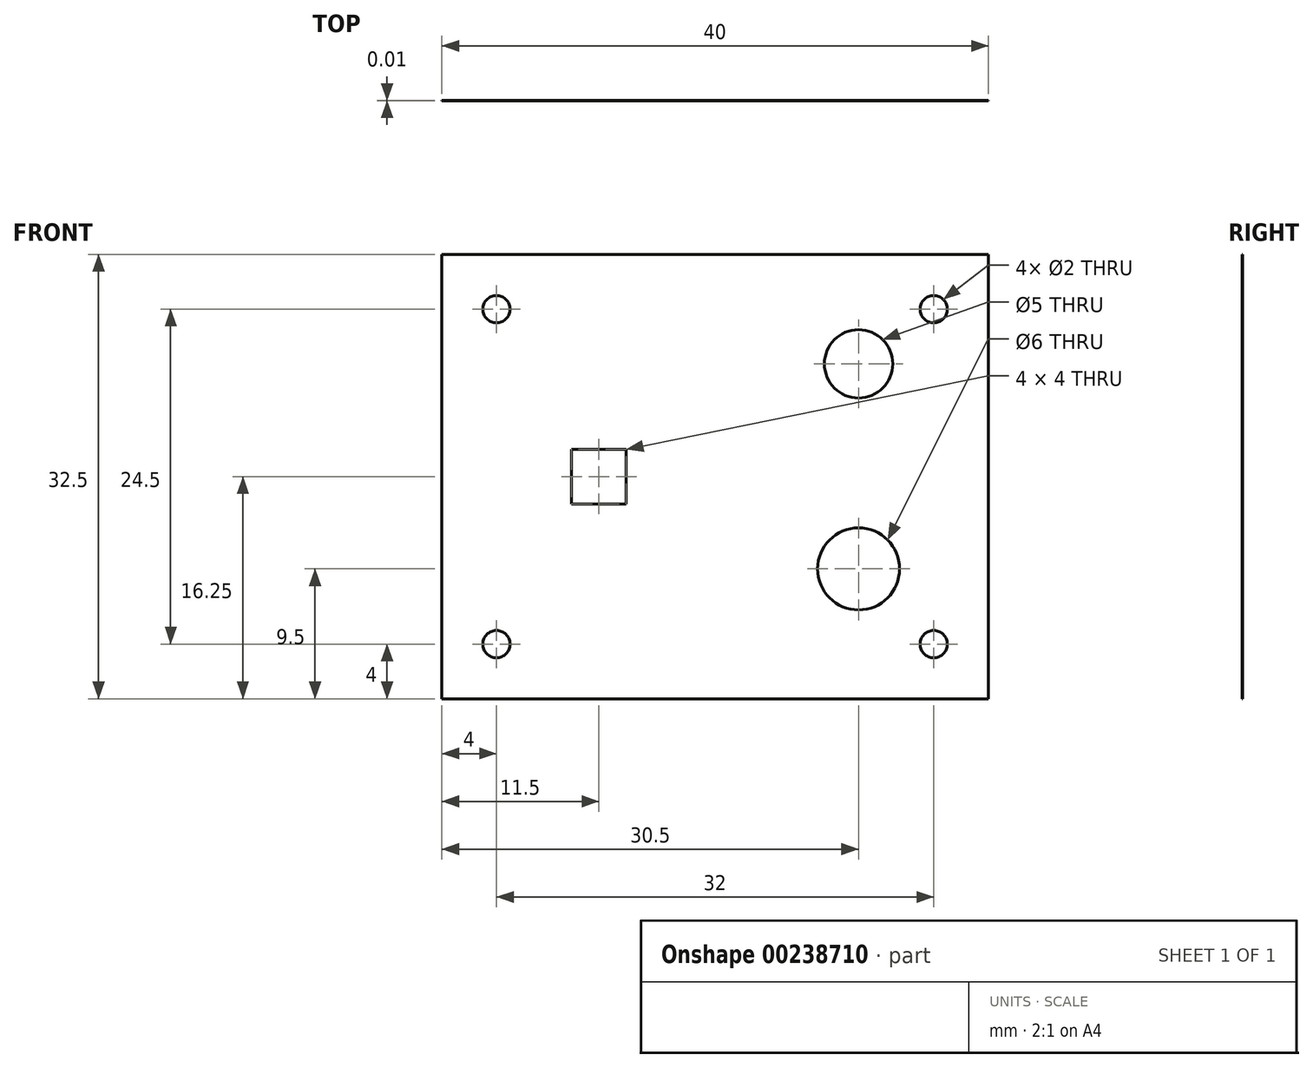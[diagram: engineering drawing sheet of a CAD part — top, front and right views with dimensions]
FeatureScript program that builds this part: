
annotation { "Feature Type Name" : "Feature", "Feature Type Description" : "" }
export const myFeature = defineFeature(function(context is Context, id is Id, definition is map)
    precondition{}
    {
        {
            var Q0;
            Q0=qCreatedBy(makeId("Front.planeOp"),FACE);
            var sketch = newSketch(context, id + "F0", { "sketchPlane" : qUnion([Q0])});
            skCircle(sketch, "E0", {"center": v(31.5, 16.25) * mm, "radius": 6.5 * mm, "construction": true});
            skCircle(sketch, "E1", {"center": v(50.5, 9.5) * mm, "radius": 4.5 * mm});
            skCircle(sketch, "E2", {"center": v(50.5, 9.5) * mm, "radius": 3 * mm});
            skCircle(sketch, "E3", {"center": v(50.5, 24.5) * mm, "radius": 3 * mm});
            skCircle(sketch, "E4", {"center": v(50.5, 24.5) * mm, "radius": 2.5 * mm});
            skLineSegment(sketch, "E5", {"start": v(50.5, 27.5) * mm, "end": v(50.5, 5) * mm, "construction": true});
            skPoint(sketch, "E6.positionSnap0", {"position": v(50.5, 16.25) * mm});
            skLineSegment(sketch, "E7.bottom", {"start": v(20, 32.5) * mm, "end": v(60, 32.5) * mm});
            skLineSegment(sketch, "E7.top", {"start": v(20, 0) * mm, "end": v(60, 0) * mm});
            skLineSegment(sketch, "E7.left", {"start": v(20, 32.5) * mm, "end": v(20, 0) * mm});
            skLineSegment(sketch, "E7.right", {"start": v(60, 32.5) * mm, "end": v(60, 0) * mm});
            skLineSegment(sketch, "E8", {"start": v(25.5, 22.25) * mm, "end": v(25.5, 23.75) * mm});
            skLineSegment(sketch, "E9", {"start": v(25.5, 23.75) * mm, "end": v(37.5, 23.75) * mm});
            skLineSegment(sketch, "E10", {"start": v(37.5, 23.75) * mm, "end": v(37.5, 22.25) * mm});
            skLineSegment(sketch, "E11", {"start": v(20, 16.25) * mm, "end": v(60, 16.25) * mm, "construction": true});
            skLineSegment(sketch, "E12.MirrorCS", {"start": v(37.5, 8.75) * mm, "end": v(37.5, 10.25) * mm});
            skLineSegment(sketch, "E13.MirrorCS", {"start": v(25.5, 8.75) * mm, "end": v(37.5, 8.75) * mm});
            skLineSegment(sketch, "E14.MirrorCS", {"start": v(25.5, 10.25) * mm, "end": v(25.5, 8.75) * mm});
            skLineSegment(sketch, "E15", {"start": v(55, 9.5) * mm, "end": v(60, 9.5) * mm, "construction": true});
            skLineSegment(sketch, "E16", {"start": v(46, 9.5) * mm, "end": v(46, 16.25) * mm, "construction": true});
            skLineSegment(sketch, "E17.bottom", {"start": v(37.5, 22.25) * mm, "end": v(25.5, 22.25) * mm});
            skLineSegment(sketch, "E17.top", {"start": v(37.5, 10.25) * mm, "end": v(25.5, 10.25) * mm});
            skLineSegment(sketch, "E17.left", {"start": v(37.5, 22.25) * mm, "end": v(37.5, 10.25) * mm});
            skLineSegment(sketch, "E17.right", {"start": v(25.5, 22.25) * mm, "end": v(25.5, 10.25) * mm});
            skLineSegment(sketch, "E18.bottom", {"start": v(29.5, 18.25) * mm, "end": v(33.5, 18.25) * mm});
            skLineSegment(sketch, "E18.top", {"start": v(29.5, 14.25) * mm, "end": v(33.5, 14.25) * mm});
            skLineSegment(sketch, "E18.left", {"start": v(29.5, 18.25) * mm, "end": v(29.5, 14.25) * mm});
            skLineSegment(sketch, "E18.right", {"start": v(33.5, 18.25) * mm, "end": v(33.5, 14.25) * mm});
            skLineSegment(sketch, "E19.1.0.0", {"start": v(97.5, 22.25) * mm, "end": v(85.5, 22.25) * mm});
            skCircle(sketch, "E19.1.0.1", {"center": v(110.5, 24.5) * mm, "radius": 2.5 * mm});
            skCircle(sketch, "E19.1.0.3", {"center": v(91.5, 16.25) * mm, "radius": 6.5 * mm, "construction": true});
            skLineSegment(sketch, "E19.1.0.4", {"start": v(120, 32.5) * mm, "end": v(120, 0) * mm});
            skLineSegment(sketch, "E19.1.0.5", {"start": v(80, 32.5) * mm, "end": v(120, 32.5) * mm});
            skLineSegment(sketch, "E19.1.0.6", {"start": v(89.5, 18.25) * mm, "end": v(89.5, 14.25) * mm});
            skLineSegment(sketch, "E19.1.0.7", {"start": v(89.5, 18.25) * mm, "end": v(93.5, 18.25) * mm});
            skLineSegment(sketch, "E19.1.0.8", {"start": v(97.5, 10.25) * mm, "end": v(85.5, 10.25) * mm});
            skLineSegment(sketch, "E19.1.0.9", {"start": v(85.5, 23.75) * mm, "end": v(97.5, 23.75) * mm});
            skCircle(sketch, "E19.1.0.10", {"center": v(110.5, 9.5) * mm, "radius": 4.5 * mm});
            skLineSegment(sketch, "E19.1.0.11", {"start": v(93.5, 18.25) * mm, "end": v(93.5, 14.25) * mm});
            skPoint(sketch, "E19.1.0.13", {"position": v(91.5, 16.25) * mm});
            skLineSegment(sketch, "E19.1.0.14", {"start": v(80, 32.5) * mm, "end": v(80, 0) * mm});
            skLineSegment(sketch, "E19.1.0.15", {"start": v(85.5, 8.75) * mm, "end": v(97.5, 8.75) * mm});
            skCircle(sketch, "E19.1.0.16", {"center": v(110.5, 9.5) * mm, "radius": 3 * mm});
            skCircle(sketch, "E19.1.0.17", {"center": v(110.5, 24.5) * mm, "radius": 3 * mm});
            skLineSegment(sketch, "E19.1.0.18", {"start": v(85.5, 22.25) * mm, "end": v(85.5, 10.25) * mm});
            skLineSegment(sketch, "E19.1.0.19", {"start": v(97.5, 22.25) * mm, "end": v(97.5, 10.25) * mm});
            skLineSegment(sketch, "E19.1.0.20", {"start": v(80, 0) * mm, "end": v(120, 0) * mm});
            skLineSegment(sketch, "E19.1.0.22", {"start": v(89.5, 14.25) * mm, "end": v(93.5, 14.25) * mm});
            skPoint(sketch, "E19.1.0.23", {"position": v(91.5, 16.25) * mm});
            skLineSegment(sketch, "E19.1.0.24", {"start": v(97.5, 23.75) * mm, "end": v(97.5, 22.25) * mm});
            skLineSegment(sketch, "E19.1.0.25", {"start": v(85.5, 22.25) * mm, "end": v(85.5, 23.75) * mm});
            skLineSegment(sketch, "E19.1.0.26", {"start": v(85.5, 10.25) * mm, "end": v(85.5, 8.75) * mm});
            skLineSegment(sketch, "E19.1.0.27", {"start": v(97.5, 8.75) * mm, "end": v(97.5, 10.25) * mm});
            skLineSegment(sketch, "E19.2.0.0", {"start": v(157.5, 22.25) * mm, "end": v(145.5, 22.25) * mm});
            skCircle(sketch, "E19.2.0.1", {"center": v(170.5, 24.5) * mm, "radius": 2.5 * mm});
            skCircle(sketch, "E19.2.0.3", {"center": v(151.5, 16.25) * mm, "radius": 6.5 * mm, "construction": true});
            skLineSegment(sketch, "E19.2.0.4", {"start": v(180, 32.5) * mm, "end": v(180, 0) * mm});
            skLineSegment(sketch, "E19.2.0.5", {"start": v(140, 32.5) * mm, "end": v(180, 32.5) * mm});
            skLineSegment(sketch, "E19.2.0.6", {"start": v(149.5, 18.25) * mm, "end": v(149.5, 14.25) * mm});
            skLineSegment(sketch, "E19.2.0.7", {"start": v(149.5, 18.25) * mm, "end": v(153.5, 18.25) * mm});
            skLineSegment(sketch, "E19.2.0.8", {"start": v(157.5, 10.25) * mm, "end": v(145.5, 10.25) * mm});
            skLineSegment(sketch, "E19.2.0.9", {"start": v(145.5, 23.75) * mm, "end": v(157.5, 23.75) * mm});
            skCircle(sketch, "E19.2.0.10", {"center": v(170.5, 9.5) * mm, "radius": 4.5 * mm});
            skLineSegment(sketch, "E19.2.0.11", {"start": v(153.5, 18.25) * mm, "end": v(153.5, 14.25) * mm});
            skPoint(sketch, "E19.2.0.13", {"position": v(151.5, 16.25) * mm});
            skLineSegment(sketch, "E19.2.0.14", {"start": v(140, 32.5) * mm, "end": v(140, 0) * mm});
            skLineSegment(sketch, "E19.2.0.15", {"start": v(145.5, 8.75) * mm, "end": v(157.5, 8.75) * mm});
            skCircle(sketch, "E19.2.0.16", {"center": v(170.5, 9.5) * mm, "radius": 3 * mm});
            skCircle(sketch, "E19.2.0.17", {"center": v(170.5, 24.5) * mm, "radius": 3 * mm});
            skLineSegment(sketch, "E19.2.0.18", {"start": v(145.5, 22.25) * mm, "end": v(145.5, 10.25) * mm});
            skLineSegment(sketch, "E19.2.0.19", {"start": v(157.5, 22.25) * mm, "end": v(157.5, 10.25) * mm});
            skLineSegment(sketch, "E19.2.0.20", {"start": v(140, 0) * mm, "end": v(180, 0) * mm});
            skLineSegment(sketch, "E19.2.0.22", {"start": v(149.5, 14.25) * mm, "end": v(153.5, 14.25) * mm});
            skPoint(sketch, "E19.2.0.23", {"position": v(151.5, 16.25) * mm});
            skLineSegment(sketch, "E19.2.0.24", {"start": v(157.5, 23.75) * mm, "end": v(157.5, 22.25) * mm});
            skLineSegment(sketch, "E19.2.0.25", {"start": v(145.5, 22.25) * mm, "end": v(145.5, 23.75) * mm});
            skLineSegment(sketch, "E19.2.0.26", {"start": v(145.5, 10.25) * mm, "end": v(145.5, 8.75) * mm});
            skLineSegment(sketch, "E19.2.0.27", {"start": v(157.5, 8.75) * mm, "end": v(157.5, 10.25) * mm});
            skLineSegment(sketch, "E19.3.0.0", {"start": v(217.5, 22.25) * mm, "end": v(205.5, 22.25) * mm});
            skCircle(sketch, "E19.3.0.1", {"center": v(230.5, 24.5) * mm, "radius": 2.5 * mm});
            skCircle(sketch, "E19.3.0.3", {"center": v(211.5, 16.25) * mm, "radius": 6.5 * mm, "construction": true});
            skLineSegment(sketch, "E19.3.0.4", {"start": v(240, 32.5) * mm, "end": v(240, 0) * mm});
            skLineSegment(sketch, "E19.3.0.5", {"start": v(200, 32.5) * mm, "end": v(240, 32.5) * mm});
            skLineSegment(sketch, "E19.3.0.6", {"start": v(209.5, 18.25) * mm, "end": v(209.5, 14.25) * mm});
            skLineSegment(sketch, "E19.3.0.7", {"start": v(209.5, 18.25) * mm, "end": v(213.5, 18.25) * mm});
            skLineSegment(sketch, "E19.3.0.8", {"start": v(217.5, 10.25) * mm, "end": v(205.5, 10.25) * mm});
            skLineSegment(sketch, "E19.3.0.9", {"start": v(205.5, 23.75) * mm, "end": v(217.5, 23.75) * mm});
            skCircle(sketch, "E19.3.0.10", {"center": v(230.5, 9.5) * mm, "radius": 4.5 * mm});
            skLineSegment(sketch, "E19.3.0.11", {"start": v(213.5, 18.25) * mm, "end": v(213.5, 14.25) * mm});
            skPoint(sketch, "E19.3.0.13", {"position": v(211.5, 16.25) * mm});
            skLineSegment(sketch, "E19.3.0.14", {"start": v(200, 32.5) * mm, "end": v(200, 0) * mm});
            skLineSegment(sketch, "E19.3.0.15", {"start": v(205.5, 8.75) * mm, "end": v(217.5, 8.75) * mm});
            skCircle(sketch, "E19.3.0.16", {"center": v(230.5, 9.5) * mm, "radius": 3 * mm});
            skCircle(sketch, "E19.3.0.17", {"center": v(230.5, 24.5) * mm, "radius": 3 * mm});
            skLineSegment(sketch, "E19.3.0.18", {"start": v(205.5, 22.25) * mm, "end": v(205.5, 10.25) * mm});
            skLineSegment(sketch, "E19.3.0.19", {"start": v(217.5, 22.25) * mm, "end": v(217.5, 10.25) * mm});
            skLineSegment(sketch, "E19.3.0.20", {"start": v(200, 0) * mm, "end": v(240, 0) * mm});
            skLineSegment(sketch, "E19.3.0.22", {"start": v(209.5, 14.25) * mm, "end": v(213.5, 14.25) * mm});
            skPoint(sketch, "E19.3.0.23", {"position": v(211.5, 16.25) * mm});
            skLineSegment(sketch, "E19.3.0.24", {"start": v(217.5, 23.75) * mm, "end": v(217.5, 22.25) * mm});
            skLineSegment(sketch, "E19.3.0.25", {"start": v(205.5, 22.25) * mm, "end": v(205.5, 23.75) * mm});
            skLineSegment(sketch, "E19.3.0.26", {"start": v(205.5, 10.25) * mm, "end": v(205.5, 8.75) * mm});
            skLineSegment(sketch, "E19.3.0.27", {"start": v(217.5, 8.75) * mm, "end": v(217.5, 10.25) * mm});
            skLineSegment(sketch, "E19.direction1", {"start": v(20, 0) * mm, "end": v(80, 0) * mm, "construction": true});
            skLineSegment(sketch, "E20.bottom", {"start": v(0, -97.5) * mm, "end": v(260, -97.5) * mm});
            skLineSegment(sketch, "E20.top", {"start": v(0, 52.5) * mm, "end": v(260, 52.5) * mm});
            skLineSegment(sketch, "E20.left", {"start": v(0, -97.5) * mm, "end": v(0, 52.5) * mm});
            skLineSegment(sketch, "E20.right", {"start": v(260, -97.5) * mm, "end": v(260, 52.5) * mm});
            skLineSegment(sketch, "E21", {"start": v(120, 0) * mm, "end": v(140, 0) * mm, "construction": true});
            skLineSegment(sketch, "E22.bottom", {"start": v(149.5, -42.5) * mm, "end": v(103.5, -42.5) * mm});
            skLineSegment(sketch, "E22.top", {"start": v(149.5, -69.5) * mm, "end": v(103.5, -69.5) * mm});
            skLineSegment(sketch, "E22.right", {"start": v(103.5, -42.5) * mm, "end": v(103.5, -69.5) * mm});
            skLineSegment(sketch, "E23.bottom", {"start": v(156.5, -42.5) * mm, "end": v(150.5, -42.5) * mm});
            skLineSegment(sketch, "E23.top", {"start": v(156.5, -69.5) * mm, "end": v(150.5, -69.5) * mm});
            skLineSegment(sketch, "E23.left", {"start": v(156.5, -42.5) * mm, "end": v(156.5, -69.5) * mm});
            skLineSegment(sketch, "E24.bottom", {"start": v(157.5, -70.5) * mm, "end": v(102.5, -70.5) * mm});
            skLineSegment(sketch, "E24.top", {"start": v(157.5, -41.5) * mm, "end": v(102.5, -41.5) * mm});
            skLineSegment(sketch, "E24.left", {"start": v(157.5, -70.5) * mm, "end": v(157.5, -41.5) * mm});
            skLineSegment(sketch, "E24.right", {"start": v(102.5, -70.5) * mm, "end": v(102.5, -41.5) * mm});
            skCircle(sketch, "E25", {"center": v(148, -29.5) * mm, "radius": 5 * mm});
            skCircle(sketch, "E26", {"center": v(112, -29.5) * mm, "radius": 5 * mm});
            skLineSegment(sketch, "E27", {"start": v(148, -29.5) * mm, "end": v(112, -29.5) * mm, "construction": true});
            skLineSegment(sketch, "E28", {"start": v(150.5, -67.5) * mm, "end": v(149.5, -67.5) * mm});
            skLineSegment(sketch, "E29", {"start": v(150.5, -44.5) * mm, "end": v(149.5, -44.5) * mm});
            skLineSegment(sketch, "E30", {"start": v(150.5, -69.5) * mm, "end": v(150.5, -67.5) * mm});
            skLineSegment(sketch, "E31", {"start": v(149.5, -69.5) * mm, "end": v(149.5, -67.5) * mm});
            skLineSegment(sketch, "E32", {"start": v(150.5, -44.5) * mm, "end": v(150.5, -42.5) * mm});
            skLineSegment(sketch, "E33", {"start": v(149.5, -44.5) * mm, "end": v(149.5, -42.5) * mm});
            skLineSegment(sketch, "E34.bottom", {"start": v(100, -77.5) * mm, "end": v(100, -17.5) * mm});
            skLineSegment(sketch, "E34.top", {"start": v(160, -77.5) * mm, "end": v(160, -17.5) * mm});
            skLineSegment(sketch, "E34.left", {"start": v(100, -77.5) * mm, "end": v(160, -77.5) * mm});
            skLineSegment(sketch, "E34.right", {"start": v(100, -17.5) * mm, "end": v(160, -17.5) * mm});
            skPoint(sketch, "E35", {"position": v(130, -29.5) * mm});
            skLineSegment(sketch, "E36", {"start": v(130, -41.5) * mm, "end": v(130, -17.5) * mm, "construction": true});
            skLineSegment(sketch, "E37", {"start": v(160, -70.5) * mm, "end": v(157.5, -70.5) * mm, "construction": true});
            skLineSegment(sketch, "E38", {"start": v(102.5, -70.5) * mm, "end": v(100, -70.5) * mm, "construction": true});
            skLineSegment(sketch, "E39", {"start": v(148, -24.5) * mm, "end": v(148, -17.5) * mm, "construction": true});
            skLineSegment(sketch, "E40", {"start": v(148, -70.5) * mm, "end": v(148, -77.5) * mm, "construction": true});
            skLineSegment(sketch, "E41", {"start": v(153, -29.5) * mm, "end": v(160, -29.5) * mm, "construction": true});
            skLineSegment(sketch, "E42", {"start": v(148, -34.5) * mm, "end": v(148, -41.5) * mm, "construction": true});
            skLineSegment(sketch, "E43", {"start": v(130, 0) * mm, "end": v(130, -97.5) * mm, "construction": true});
            skLineSegment(sketch, "E44.1.0.0", {"start": v(180, -77.5) * mm, "end": v(180, -17.5) * mm});
            skLineSegment(sketch, "E44.1.0.1", {"start": v(240, -77.5) * mm, "end": v(240, -17.5) * mm});
            skLineSegment(sketch, "E44.1.0.2", {"start": v(237.5, -70.5) * mm, "end": v(182.5, -70.5) * mm});
            skLineSegment(sketch, "E44.1.0.3", {"start": v(237.5, -70.5) * mm, "end": v(237.5, -41.5) * mm});
            skLineSegment(sketch, "E44.1.0.4", {"start": v(180, -17.5) * mm, "end": v(240, -17.5) * mm});
            skLineSegment(sketch, "E44.1.0.5", {"start": v(183.5, -42.5) * mm, "end": v(183.5, -69.5) * mm});
            skPoint(sketch, "E44.1.0.6", {"position": v(210, -29.5) * mm});
            skCircle(sketch, "E44.1.0.7", {"center": v(228, -29.5) * mm, "radius": 5 * mm});
            skLineSegment(sketch, "E44.1.0.8", {"start": v(233, -29.5) * mm, "end": v(240, -29.5) * mm, "construction": true});
            skLineSegment(sketch, "E44.1.0.9", {"start": v(229.5, -69.5) * mm, "end": v(183.5, -69.5) * mm});
            skLineSegment(sketch, "E44.1.0.10", {"start": v(210, -41.5) * mm, "end": v(210, -17.5) * mm, "construction": true});
            skLineSegment(sketch, "E44.1.0.11", {"start": v(228, -70.5) * mm, "end": v(228, -77.5) * mm, "construction": true});
            skLineSegment(sketch, "E44.1.0.12", {"start": v(237.5, -41.5) * mm, "end": v(182.5, -41.5) * mm});
            skLineSegment(sketch, "E44.1.0.13", {"start": v(228, -24.5) * mm, "end": v(228, -17.5) * mm, "construction": true});
            skLineSegment(sketch, "E44.1.0.14", {"start": v(229.5, -42.5) * mm, "end": v(183.5, -42.5) * mm});
            skCircle(sketch, "E44.1.0.15", {"center": v(192, -29.5) * mm, "radius": 5 * mm});
            skLineSegment(sketch, "E44.1.0.16", {"start": v(228, -34.5) * mm, "end": v(228, -41.5) * mm, "construction": true});
            skLineSegment(sketch, "E44.1.0.17", {"start": v(180, -77.5) * mm, "end": v(240, -77.5) * mm});
            skLineSegment(sketch, "E44.1.0.18", {"start": v(236.5, -42.5) * mm, "end": v(236.5, -69.5) * mm});
            skLineSegment(sketch, "E44.1.0.19", {"start": v(182.5, -70.5) * mm, "end": v(182.5, -41.5) * mm});
            skLineSegment(sketch, "E44.1.0.20", {"start": v(228, -29.5) * mm, "end": v(192, -29.5) * mm, "construction": true});
            skLineSegment(sketch, "E44.1.0.21", {"start": v(240, -70.5) * mm, "end": v(237.5, -70.5) * mm, "construction": true});
            skLineSegment(sketch, "E44.1.0.22", {"start": v(182.5, -70.5) * mm, "end": v(180, -70.5) * mm, "construction": true});
            skLineSegment(sketch, "E44.1.0.23", {"start": v(229.5, -44.5) * mm, "end": v(229.5, -42.5) * mm});
            skLineSegment(sketch, "E44.1.0.24", {"start": v(236.5, -42.5) * mm, "end": v(230.5, -42.5) * mm});
            skLineSegment(sketch, "E44.1.0.25", {"start": v(230.5, -44.5) * mm, "end": v(230.5, -42.5) * mm});
            skLineSegment(sketch, "E44.1.0.26", {"start": v(236.5, -69.5) * mm, "end": v(230.5, -69.5) * mm});
            skLineSegment(sketch, "E44.1.0.27", {"start": v(230.5, -69.5) * mm, "end": v(230.5, -67.5) * mm});
            skLineSegment(sketch, "E44.1.0.28", {"start": v(230.5, -44.5) * mm, "end": v(229.5, -44.5) * mm});
            skLineSegment(sketch, "E44.1.0.29", {"start": v(229.5, -69.5) * mm, "end": v(229.5, -67.5) * mm});
            skLineSegment(sketch, "E44.1.0.30", {"start": v(230.5, -67.5) * mm, "end": v(229.5, -67.5) * mm});
            skLineSegment(sketch, "E44.direction1", {"start": v(100, -77.5) * mm, "end": v(180, -77.5) * mm, "construction": true});
            skLineSegment(sketch, "E45.bottom", {"start": v(45, -28) * mm, "end": v(45, -74) * mm});
            skLineSegment(sketch, "E45.top", {"start": v(72, -28) * mm, "end": v(72, -74) * mm});
            skLineSegment(sketch, "E45.right", {"start": v(45, -74) * mm, "end": v(72, -74) * mm});
            skLineSegment(sketch, "E46.bottom", {"start": v(45, -21) * mm, "end": v(45, -27) * mm});
            skLineSegment(sketch, "E46.top", {"start": v(72, -21) * mm, "end": v(72, -27) * mm});
            skLineSegment(sketch, "E46.left", {"start": v(45, -21) * mm, "end": v(72, -21) * mm});
            skLineSegment(sketch, "E47.bottom", {"start": v(73, -20) * mm, "end": v(73, -75) * mm});
            skLineSegment(sketch, "E47.top", {"start": v(44, -20) * mm, "end": v(44, -75) * mm});
            skLineSegment(sketch, "E47.left", {"start": v(73, -20) * mm, "end": v(44, -20) * mm});
            skLineSegment(sketch, "E47.right", {"start": v(73, -75) * mm, "end": v(44, -75) * mm});
            skCircle(sketch, "E48", {"center": v(32, -29.5) * mm, "radius": 5 * mm});
            skCircle(sketch, "E49", {"center": v(32, -65.5) * mm, "radius": 5 * mm});
            skLineSegment(sketch, "E50", {"start": v(32, -29.5) * mm, "end": v(32, -65.5) * mm, "construction": true});
            skLineSegment(sketch, "E51", {"start": v(70, -27) * mm, "end": v(70, -28) * mm});
            skLineSegment(sketch, "E52", {"start": v(47, -27) * mm, "end": v(47, -28) * mm});
            skLineSegment(sketch, "E53", {"start": v(72, -27) * mm, "end": v(70, -27) * mm});
            skLineSegment(sketch, "E54", {"start": v(72, -28) * mm, "end": v(70, -28) * mm});
            skLineSegment(sketch, "E55", {"start": v(47, -27) * mm, "end": v(45, -27) * mm});
            skLineSegment(sketch, "E56", {"start": v(47, -28) * mm, "end": v(45, -28) * mm});
            skLineSegment(sketch, "E57.bottom", {"start": v(80, -77.5) * mm, "end": v(20, -77.5) * mm});
            skLineSegment(sketch, "E57.top", {"start": v(80, -17.5) * mm, "end": v(20, -17.5) * mm});
            skLineSegment(sketch, "E57.left", {"start": v(80, -77.5) * mm, "end": v(80, -17.5) * mm});
            skLineSegment(sketch, "E57.right", {"start": v(20, -77.5) * mm, "end": v(20, -17.5) * mm});
            skPoint(sketch, "E58", {"position": v(32, -47.5) * mm});
            skLineSegment(sketch, "E59", {"start": v(44, -47.5) * mm, "end": v(20, -47.5) * mm, "construction": true});
            skLineSegment(sketch, "E60", {"start": v(73, -17.5) * mm, "end": v(73, -20) * mm, "construction": true});
            skLineSegment(sketch, "E61", {"start": v(73, -75) * mm, "end": v(73, -77.5) * mm, "construction": true});
            skLineSegment(sketch, "E62", {"start": v(27, -29.5) * mm, "end": v(20, -29.5) * mm, "construction": true});
            skLineSegment(sketch, "E63", {"start": v(73, -29.5) * mm, "end": v(80, -29.5) * mm, "construction": true});
            skLineSegment(sketch, "E64", {"start": v(32, -24.5) * mm, "end": v(32, -17.5) * mm, "construction": true});
            skLineSegment(sketch, "E65", {"start": v(37, -29.5) * mm, "end": v(44, -29.5) * mm, "construction": true});
            skCircle(sketch, "E66", {"center": v(24, 28.5) * mm, "radius": 1 * mm});
            skCircle(sketch, "E67", {"center": v(56, 28.5) * mm, "radius": 1 * mm});
            skCircle(sketch, "E68", {"center": v(56, 4) * mm, "radius": 1 * mm});
            skCircle(sketch, "E69", {"center": v(24, 4) * mm, "radius": 1 * mm});
            skCircle(sketch, "E70", {"center": v(24, -21.5) * mm, "radius": 1 * mm});
            skCircle(sketch, "E71", {"center": v(76, -21.5) * mm, "radius": 1 * mm});
            skCircle(sketch, "E72", {"center": v(24, -73.5) * mm, "radius": 1 * mm});
            skCircle(sketch, "E73", {"center": v(76, -73.5) * mm, "radius": 1 * mm});
            skCircle(sketch, "E74.1.0.0", {"center": v(84, 28.5) * mm, "radius": 1 * mm});
            skCircle(sketch, "E74.1.0.1", {"center": v(84, 4) * mm, "radius": 1 * mm});
            skCircle(sketch, "E74.1.0.2", {"center": v(116, 4) * mm, "radius": 1 * mm});
            skCircle(sketch, "E74.1.0.3", {"center": v(116, 28.5) * mm, "radius": 1 * mm});
            skCircle(sketch, "E74.2.0.0", {"center": v(144, 28.5) * mm, "radius": 1 * mm});
            skCircle(sketch, "E74.2.0.1", {"center": v(144, 4) * mm, "radius": 1 * mm});
            skCircle(sketch, "E74.2.0.2", {"center": v(176, 4) * mm, "radius": 1 * mm});
            skCircle(sketch, "E74.2.0.3", {"center": v(176, 28.5) * mm, "radius": 1 * mm});
            skCircle(sketch, "E74.3.0.0", {"center": v(204, 28.5) * mm, "radius": 1 * mm});
            skCircle(sketch, "E74.3.0.1", {"center": v(204, 4) * mm, "radius": 1 * mm});
            skCircle(sketch, "E74.3.0.2", {"center": v(236, 4) * mm, "radius": 1 * mm});
            skCircle(sketch, "E74.3.0.3", {"center": v(236, 28.5) * mm, "radius": 1 * mm});
            skLineSegment(sketch, "E74.direction1", {"start": v(24, 4) * mm, "end": v(84, 4) * mm, "construction": true});
            skCircle(sketch, "E75.1.0.0", {"center": v(104, -73.5) * mm, "radius": 1 * mm});
            skCircle(sketch, "E75.1.0.1", {"center": v(156, -73.5) * mm, "radius": 1 * mm});
            skCircle(sketch, "E75.1.0.2", {"center": v(156, -21.5) * mm, "radius": 1 * mm});
            skCircle(sketch, "E75.1.0.3", {"center": v(104, -21.5) * mm, "radius": 1 * mm});
            skCircle(sketch, "E75.2.0.0", {"center": v(184, -73.5) * mm, "radius": 1 * mm});
            skCircle(sketch, "E75.2.0.1", {"center": v(236, -73.5) * mm, "radius": 1 * mm});
            skCircle(sketch, "E75.2.0.2", {"center": v(236, -21.5) * mm, "radius": 1 * mm});
            skCircle(sketch, "E75.2.0.3", {"center": v(184, -21.5) * mm, "radius": 1 * mm});
            skLineSegment(sketch, "E75.direction1", {"start": v(24, -73.5) * mm, "end": v(104, -73.5) * mm, "construction": true});
            skSolve(sketch);
        }
        {
            var Q0;
            Q0=makeQuery(id+"F0.imprint","IMPRINT",FACE,{"disambiguationData":[TD([[makeQuery(id+"F0.imprint","IMPRINT",EDGE,{"derivedFrom":sQuery(id+"F0.wireOp",EDGE,"E1")}),-1.0]])]});
            var Q1;
            Q1=makeQuery(id+"F0.imprint","IMPRINT",FACE,{"disambiguationData":[TD([[makeQuery(id+"F0.imprint","IMPRINT",EDGE,{"derivedFrom":sQuery(id+"F0.wireOp",EDGE,"E17.bottom")}),1.0]])]});
            var Q2;
            Q2=makeQuery(id+"F0.imprint","IMPRINT",FACE,{"disambiguationData":[TD([[makeQuery(id+"F0.imprint","IMPRINT",EDGE,{"derivedFrom":sQuery(id+"F0.wireOp",EDGE,"E12.MirrorCS")}),1.0]])]});
            var Q3;
            Q3=makeQuery(id+"F0.imprint","IMPRINT",FACE,{"disambiguationData":[TD([[makeQuery(id+"F0.imprint","IMPRINT",EDGE,{"derivedFrom":sQuery(id+"F0.wireOp",EDGE,"E8")}),-1.0]])]});
            var Q4;
            Q4=makeQuery(id+"F0.imprint","IMPRINT",FACE,{"disambiguationData":[TD([[makeQuery(id+"F0.imprint","IMPRINT",EDGE,{"derivedFrom":sQuery(id+"F0.wireOp",EDGE,"E1")}),1.0]])]});
            var Q5;
            Q5=makeQuery(id+"F0.imprint","IMPRINT",FACE,{"disambiguationData":[TD([[makeQuery(id+"F0.imprint","IMPRINT",EDGE,{"derivedFrom":sQuery(id+"F0.wireOp",EDGE,"E3")}),1.0]])]});
            extrude(context, id + "F1", {"entities" : qUnion([Q0, Q1, Q2, Q3, Q4, Q5]), "oppositeDirection" : true, "depth" : 0.01 * mm});
        }
    });
